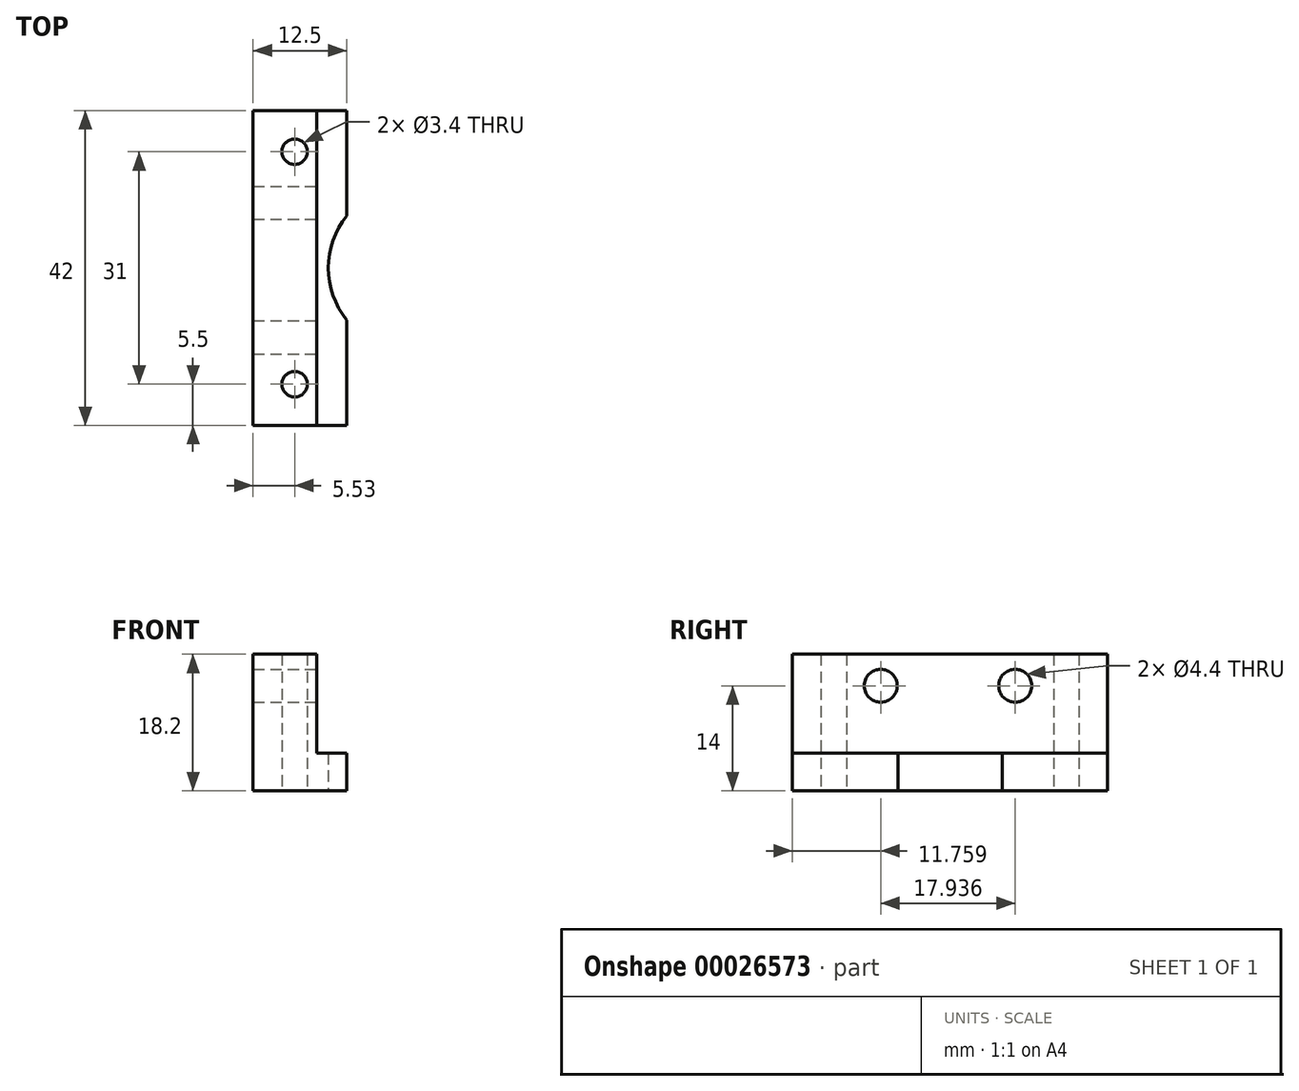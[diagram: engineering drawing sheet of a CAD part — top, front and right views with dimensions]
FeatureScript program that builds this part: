
annotation { "Feature Type Name" : "Feature", "Feature Type Description" : "" }
export const myFeature = defineFeature(function(context is Context, id is Id, definition is map)
    precondition{}
    {
        {
            var Q0;
            Q0=qCreatedBy(makeId("Front.planeOp"),FACE);
            var sketch = newSketch(context, id + "F0", { "sketchPlane" : qUnion([Q0])});
            skLineSegment(sketch, "E0", {"start": v(8.5, 18.2) * mm, "end": v(8.5, 5) * mm});
            skLineSegment(sketch, "E1", {"start": v(8.5, 5) * mm, "end": v(12.5, 5) * mm});
            skLineSegment(sketch, "E2", {"start": v(12.5, 5) * mm, "end": v(12.5, 0) * mm});
            skLineSegment(sketch, "E3", {"start": v(12.5, 0) * mm, "end": v(0, 0) * mm});
            skLineSegment(sketch, "E4", {"start": v(0, 0) * mm, "end": v(0, 18.2) * mm});
            skLineSegment(sketch, "E5", {"start": v(0, 18.2) * mm, "end": v(8.5, 18.2) * mm});
            skSolve(sketch);
        }
        {
            var Q0;
            Q0=qSketchRegion(id+"F0",true);
            extrude(context, id + "F1", {"entities" : qUnion([Q0]), "oppositeDirection" : true, "depth" : 42 * mm});
        }
        {
            var Q0;
            Q0=makeQuery(id+"F1.opExtrude","SWEPT_FACE",FACE,{"disambiguationData":[OSD([sQuery(id+"F0.wireOp",EDGE,"E3")])]});
            var sketch = newSketch(context, id + "F2", { "sketchPlane" : qUnion([Q0])});
            skCircle(sketch, "E6", {"center": v(5.53, -5.5) * mm, "radius": 1.7 * mm});
            skCircle(sketch, "E7", {"center": v(5.53, -36.5) * mm, "radius": 1.7 * mm});
            skCircle(sketch, "E8", {"center": v(21.03, -21) * mm, "radius": 11 * mm});
            skLineSegment(sketch, "E9", {"start": v(0, -21) * mm, "end": v(12.5, -21) * mm, "construction": true});
            skSolve(sketch);
        }
        {
            var Q0;
            Q0=qSketchRegion(id+"F2",true);
            extrude(context, id + "F3", {"entities" : qUnion([Q0]), "operationType" : NewBodyOperationType.REMOVE, "endBound" : BoundingType.THROUGH_ALL, "oppositeDirection" : true, "depth" : 25 * mm});
        }
        {
            var Q0;
            Q0=makeQuery(id+"F1.opExtrude","SWEPT_FACE",FACE,{"disambiguationData":[OSD([sQuery(id+"F0.wireOp",EDGE,"E0")])]});
            var sketch = newSketch(context, id + "F4", { "sketchPlane" : qUnion([Q0])});
            skCircle(sketch, "E10", {"center": v(11.76, 14) * mm, "radius": 2.2 * mm});
            skCircle(sketch, "E11", {"center": v(29.7, 14) * mm, "radius": 2.2 * mm});
            skPoint(sketch, "E12", {"position": v(7.56, 18.2) * mm});
            skPoint(sketch, "E13", {"position": v(33.9, 18.2) * mm});
            skLineSegment(sketch, "E14", {"start": v(7.56, 18.2) * mm, "end": v(7.56, 10.72) * mm, "construction": true});
            skLineSegment(sketch, "E15", {"start": v(33.9, 18.2) * mm, "end": v(33.9, 12.44) * mm, "construction": true});
            skSolve(sketch);
        }
        {
            var Q0;
            Q0=qSketchRegion(id+"F4",true);
            extrude(context, id + "F5", {"entities" : qUnion([Q0]), "operationType" : NewBodyOperationType.REMOVE, "oppositeDirection" : true, "depth" : 25 * mm});
        }
    });
